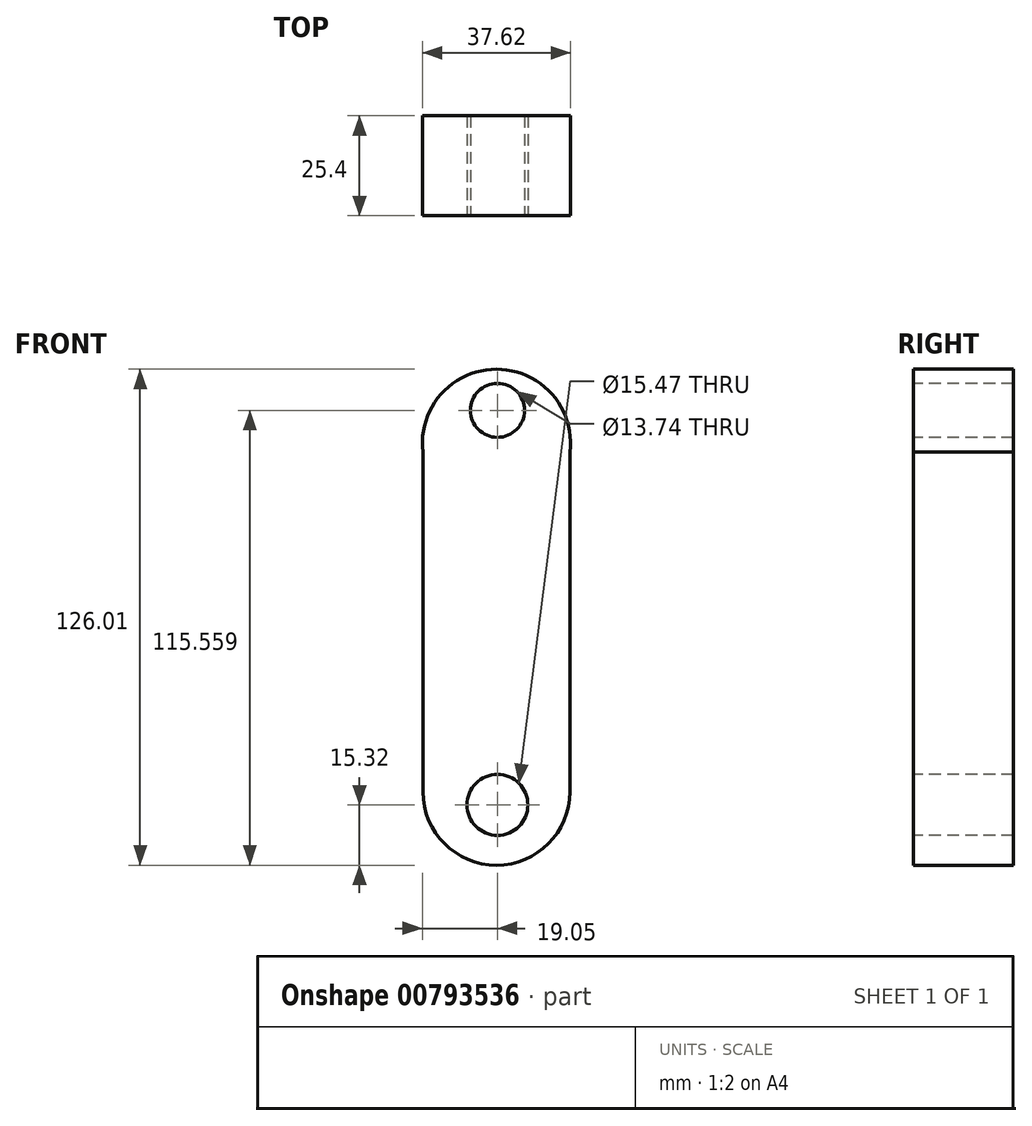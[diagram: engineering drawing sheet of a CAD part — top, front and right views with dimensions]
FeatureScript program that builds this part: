
annotation { "Feature Type Name" : "Feature", "Feature Type Description" : "" }
export const myFeature = defineFeature(function(context is Context, id is Id, definition is map)
    precondition{}
    {
        {
            var Q0;
            Q0=qCreatedBy(makeId("Front.planeOp"),FACE);
            var sketch = newSketch(context, id + "F0", { "sketchPlane" : qUnion([Q0])});
            skLineSegment(sketch, "E0.bottom", {"start": v(-18.92, 46.63) * mm, "end": v(18.44, 46.63) * mm});
            skLineSegment(sketch, "E0.top", {"start": v(-18.92, -39.64) * mm, "end": v(18.44, -39.64) * mm});
            skLineSegment(sketch, "E0.left", {"start": v(-18.92, 46.63) * mm, "end": v(-18.92, -39.64) * mm});
            skLineSegment(sketch, "E0.right", {"start": v(18.44, 46.63) * mm, "end": v(18.44, -39.64) * mm});
            skArc(sketch, "E1", {"start": v(18.44, 46.63) * mm, "mid": v(-0.24, 67.69) * mm, "end": v(-18.92, 46.63) * mm});
            skArc(sketch, "E2", {"start": v(-18.92, -39.64) * mm, "mid": v(-0.24, -58.32) * mm, "end": v(18.44, -39.64) * mm});
            skSolve(sketch);
        }
        {
            var Q0;
            Q0=makeQuery(id+"F0.imprint","IMPRINT",FACE,{"disambiguationData":[TD([[makeQuery(id+"F0.imprint","IMPRINT",EDGE,{"derivedFrom":sQuery(id+"F0.wireOp",EDGE,"E0.bottom")}),1.0]])]});
            var Q1;
            Q1=makeQuery(id+"F0.imprint","IMPRINT",FACE,{"disambiguationData":[TD([[makeQuery(id+"F0.imprint","IMPRINT",EDGE,{"derivedFrom":sQuery(id+"F0.wireOp",EDGE,"E0.bottom")}),-1.0]])]});
            var Q2;
            Q2=makeQuery(id+"F0.imprint","IMPRINT",FACE,{"disambiguationData":[TD([[makeQuery(id+"F0.imprint","IMPRINT",EDGE,{"derivedFrom":sQuery(id+"F0.wireOp",EDGE,"E0.top")}),-1.0]])]});
            extrude(context, id + "F1", {"entities" : qUnion([Q0, Q1, Q2]), "depth" : 25.4 * mm, "offsetDistance" : 25.4 * mm});
        }
        {
            var Q0;
            Q0=makeQuery(id+"F1.opExtrude","CAP_FACE",FACE,{"disambiguationData":[OSD([sQuery(id+"F0.wireOp",EDGE,"E0.left"),sQuery(id+"F0.wireOp",EDGE,"E0.right"),sQuery(id+"F0.wireOp",EDGE,"E1"),sQuery(id+"F0.wireOp",EDGE,"E2")])],"isStart":false});
            var sketch = newSketch(context, id + "F2", { "sketchPlane" : qUnion([Q0])});
            skCircle(sketch, "E3", {"center": v(0, 57.24) * mm, "radius": 6.87 * mm});
            skCircle(sketch, "E4", {"center": v(0, -43) * mm, "radius": 7.74 * mm});
            skSolve(sketch);
        }
        {
            var Q0;
            Q0=makeQuery(id+"F2.imprint","IMPRINT",FACE,{"disambiguationData":[TD([[makeQuery(id+"F2.imprint","IMPRINT",EDGE,{"derivedFrom":sQuery(id+"F2.wireOp",EDGE,"E3")}),1.0]])]});
            var Q1;
            Q1=makeQuery(id+"F2.imprint","IMPRINT",FACE,{"disambiguationData":[TD([[makeQuery(id+"F2.imprint","IMPRINT",EDGE,{"derivedFrom":sQuery(id+"F2.wireOp",EDGE,"E4")}),1.0]])]});
            extrude(context, id + "F3", {"entities" : qUnion([Q0, Q1]), "operationType" : NewBodyOperationType.REMOVE, "oppositeDirection" : true, "depth" : 25.4 * mm, "offsetDistance" : 25.4 * mm});
        }
    });
